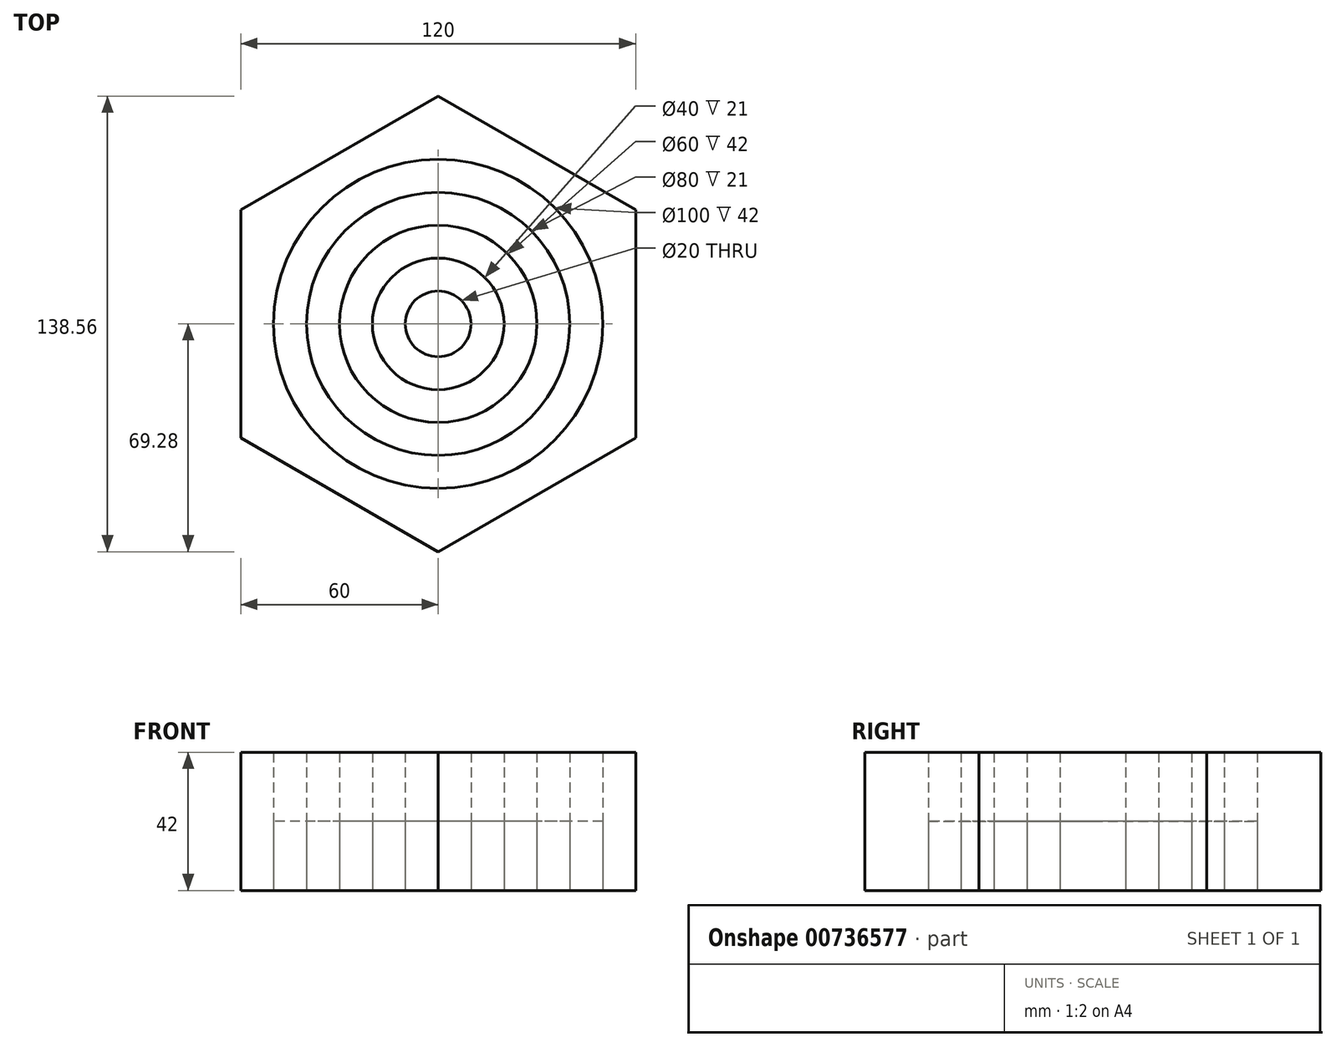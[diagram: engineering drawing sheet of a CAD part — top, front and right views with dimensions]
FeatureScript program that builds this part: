
annotation { "Feature Type Name" : "Feature", "Feature Type Description" : "" }
export const myFeature = defineFeature(function(context is Context, id is Id, definition is map)
    precondition{}
    {
        {
            var Q0;
            Q0=qCreatedBy(makeId("Top.planeOp"),FACE);
            var sketch = newSketch(context, id + "F0", { "sketchPlane" : qUnion([Q0])});
            skCircle(sketch, "E0.cCircle", {"center": v(0, 0) * mm, "radius": 60 * mm, "construction": true});
            skLineSegment(sketch, "E0.0", {"start": v(60, 34.64) * mm, "end": v(60, -34.64) * mm});
            skLineSegment(sketch, "E0.1", {"start": v(60, -34.64) * mm, "end": v(0, -69.28) * mm});
            skLineSegment(sketch, "E0.2", {"start": v(0, -69.28) * mm, "end": v(-60, -34.64) * mm});
            skLineSegment(sketch, "E0.3", {"start": v(-60, -34.64) * mm, "end": v(-60, 34.64) * mm});
            skLineSegment(sketch, "E0.4", {"start": v(-60, 34.64) * mm, "end": v(0, 69.28) * mm});
            skLineSegment(sketch, "E0.5", {"start": v(0, 69.28) * mm, "end": v(60, 34.64) * mm});
            skPoint(sketch, "E0.0.midPoint", {"position": v(60, 0) * mm});
            skCircle(sketch, "E1", {"center": v(0, 0) * mm, "radius": 50 * mm});
            skCircle(sketch, "E2", {"center": v(0, 0) * mm, "radius": 40 * mm});
            skCircle(sketch, "E3", {"center": v(0, 0) * mm, "radius": 30 * mm});
            skCircle(sketch, "E4", {"center": v(0, 0) * mm, "radius": 20 * mm});
            skCircle(sketch, "E5", {"center": v(0, 0) * mm, "radius": 10 * mm});
            skSolve(sketch);
        }
        {
            var Q0;
            Q0=makeQuery(id+"F0.imprint","IMPRINT",FACE,{"disambiguationData":[TD([[makeQuery(id+"F0.imprint","IMPRINT",EDGE,{"derivedFrom":sQuery(id+"F0.wireOp",EDGE,"E0.0")}),-1.0]])]});
            var Q1;
            Q1=makeQuery(id+"F0.imprint","IMPRINT",FACE,{"disambiguationData":[TD([[makeQuery(id+"F0.imprint","IMPRINT",EDGE,{"derivedFrom":sQuery(id+"F0.wireOp",EDGE,"E2")}),1.0]])]});
            var Q2;
            Q2=makeQuery(id+"F0.imprint","IMPRINT",FACE,{"disambiguationData":[TD([[makeQuery(id+"F0.imprint","IMPRINT",EDGE,{"derivedFrom":sQuery(id+"F0.wireOp",EDGE,"E4")}),1.0]])]});
            extrude(context, id + "F1", {"entities" : qUnion([Q0, Q1, Q2]), "depth" : 42 * mm, "offsetDistance" : 25 * mm});
        }
        {
            var Q0;
            Q0=makeQuery(id+"F0.imprint","IMPRINT",FACE,{"disambiguationData":[TD([[makeQuery(id+"F0.imprint","IMPRINT",EDGE,{"derivedFrom":sQuery(id+"F0.wireOp",EDGE,"E1")}),1.0]])]});
            var Q1;
            Q1=makeQuery(id+"F0.imprint","IMPRINT",FACE,{"disambiguationData":[TD([[makeQuery(id+"F0.imprint","IMPRINT",EDGE,{"derivedFrom":sQuery(id+"F0.wireOp",EDGE,"E3")}),1.0]])]});
            var Q2;
            Q2=makeQuery(id+"F0.imprint","IMPRINT",FACE,{"disambiguationData":[TD([[makeQuery(id+"F0.imprint","IMPRINT",EDGE,{"derivedFrom":sQuery(id+"F0.wireOp",EDGE,"E5")}),1.0]])]});
            extrude(context, id + "F2", {"entities" : qUnion([Q0, Q1, Q2]), "depth" : 21 * mm, "offsetDistance" : 25 * mm});
        }
    });
